# Revit family: Vanity-American_Standard-Townsend-0330.000-9036.030
name_source: partatom
category: Plumbing Fixtures
revit_build: Autodesk Revit 2014 (Build: 20130308_1515(x64)
units: mm (PartAtom-declared; Revit-internal decimal feet)

## types (1)
- 0330.000-7840.800.820-9036.030
    7720.018 Optional Decorative P-trap Drain. = No
    7760.000 - Drawer Pulls For 30" Vanity. = Yes
    7840.800.820 - Quartz Top With 8" Center Faucet Holes. = Yes
    Assembly Code = E2020200
    CW Connection = Yes
    CWFU = 1.5
    Cold Water Connection Diameter = 0' - 0 1/2"
    Default Elevation = 0' - 0"
    Description = American Standard Furinture For Townsend Sinks 30" Vanity
    HW Connection = Yes
    HWFU = 1.5
    Height = 2' - 10"
    Hole Location = 0' - 10"
    Hole Width = 0' - 8"
    Hot Water Connection Diameter = 0' - 0 1/2"
    Length = 2' - 6"
    Manufacturer = American Standard
    Material = Vitreous China-American Standard-020-White
    Model = 0330.000-7840.800.820-9036.030
    Product Page URL = https://www.americanstandard-us.com
    URL = https://www.americanstandard-us.com
    Vent Connection = No
    WFU = 2
    Warranty Information = 1 Year Limited Warranty
    Waste Connection = Yes
    Waste Connection Diameter = 0' - 1 1/4"
    Width = 1' - 8"

## geometry (parser evidence)
native form markers: Sweep x2
no freeform markers — native parametric forms only
